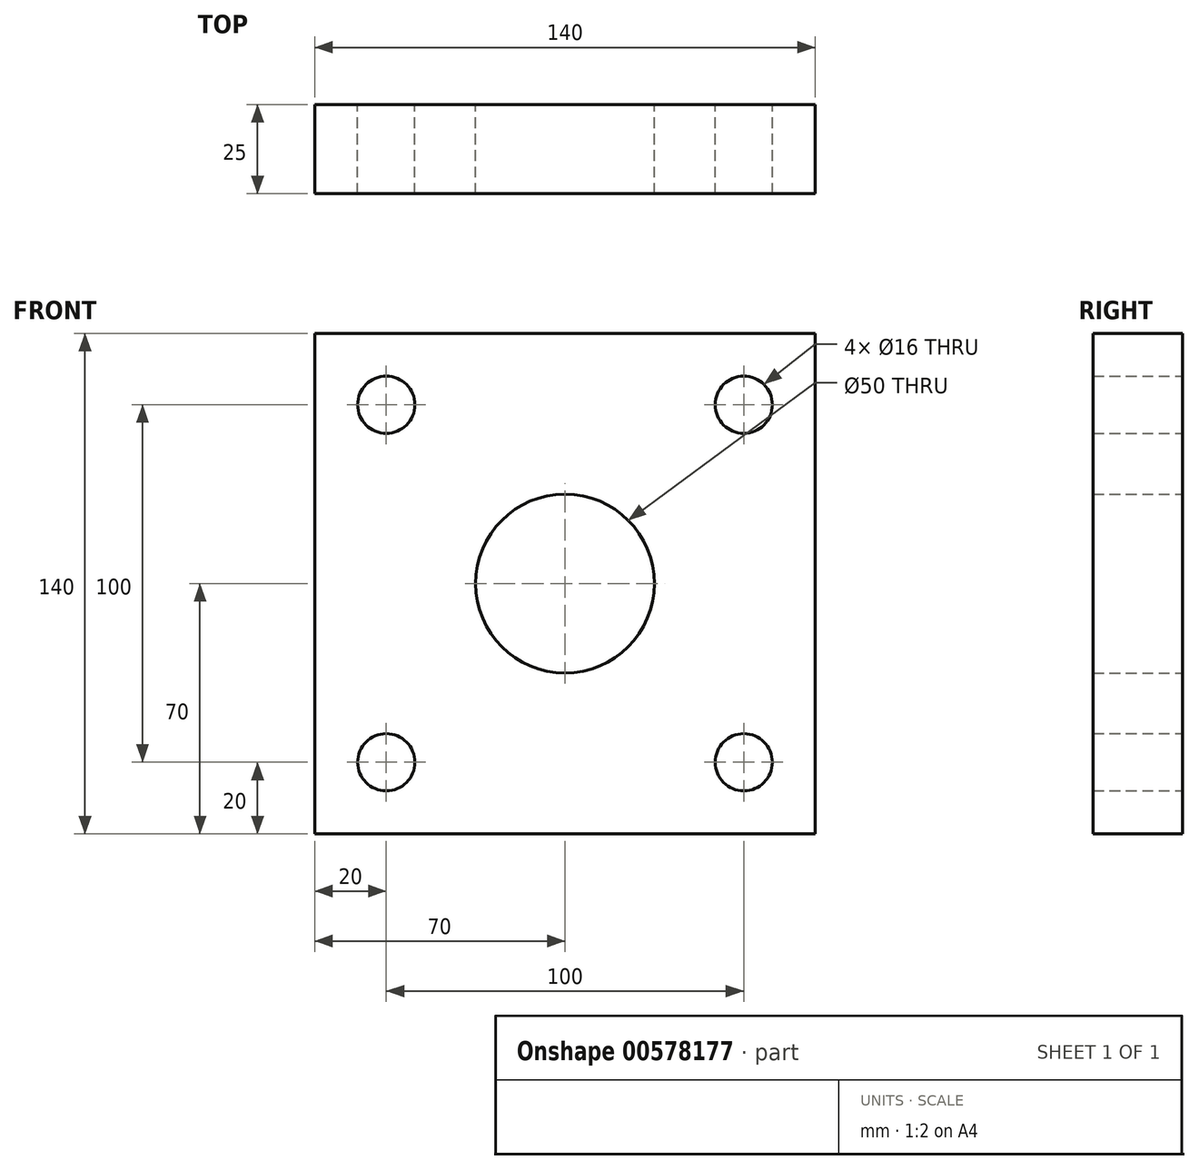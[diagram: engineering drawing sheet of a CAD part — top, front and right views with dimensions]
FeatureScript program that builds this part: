
annotation { "Feature Type Name" : "Feature", "Feature Type Description" : "" }
export const myFeature = defineFeature(function(context is Context, id is Id, definition is map)
    precondition{}
    {
        {
            var Q0;
            Q0=qCreatedBy(makeId("Front.planeOp"),FACE);
            var sketch = newSketch(context, id + "F0", { "sketchPlane" : qUnion([Q0])});
            skLineSegment(sketch, "E0.bottom", {"start": v(-70, 70) * mm, "end": v(70, 70) * mm});
            skLineSegment(sketch, "E0.top", {"start": v(-70, -70) * mm, "end": v(70, -70) * mm});
            skLineSegment(sketch, "E0.left", {"start": v(-70, 70) * mm, "end": v(-70, -70) * mm});
            skLineSegment(sketch, "E0.right", {"start": v(70, 70) * mm, "end": v(70, -70) * mm});
            skLineSegment(sketch, "E1.bottom", {"start": v(-50, 50) * mm, "end": v(50, 50) * mm, "construction": true});
            skLineSegment(sketch, "E1.top", {"start": v(-50, -50) * mm, "end": v(50, -50) * mm, "construction": true});
            skLineSegment(sketch, "E1.left", {"start": v(-50, 50) * mm, "end": v(-50, -50) * mm, "construction": true});
            skLineSegment(sketch, "E1.right", {"start": v(50, 50) * mm, "end": v(50, -50) * mm, "construction": true});
            skCircle(sketch, "E2", {"center": v(-50, 50) * mm, "radius": 8 * mm});
            skCircle(sketch, "E3", {"center": v(50, 50) * mm, "radius": 8 * mm});
            skCircle(sketch, "E4", {"center": v(-50, -50) * mm, "radius": 8 * mm});
            skCircle(sketch, "E5", {"center": v(50, -50) * mm, "radius": 8 * mm});
            skCircle(sketch, "E6", {"center": v(0, 0) * mm, "radius": 25 * mm});
            skSolve(sketch);
        }
        {
            var Q0;
            Q0=makeQuery(id+"F0.imprint","IMPRINT",FACE,{"disambiguationData":[TD([[makeQuery(id+"F0.imprint","IMPRINT",EDGE,{"derivedFrom":sQuery(id+"F0.wireOp",EDGE,"E0.bottom")}),-1.0]])]});
            extrude(context, id + "F1", {"entities" : qUnion([Q0]), "depth" : 25 * mm, "offsetDistance" : 25 * mm});
        }
    });
